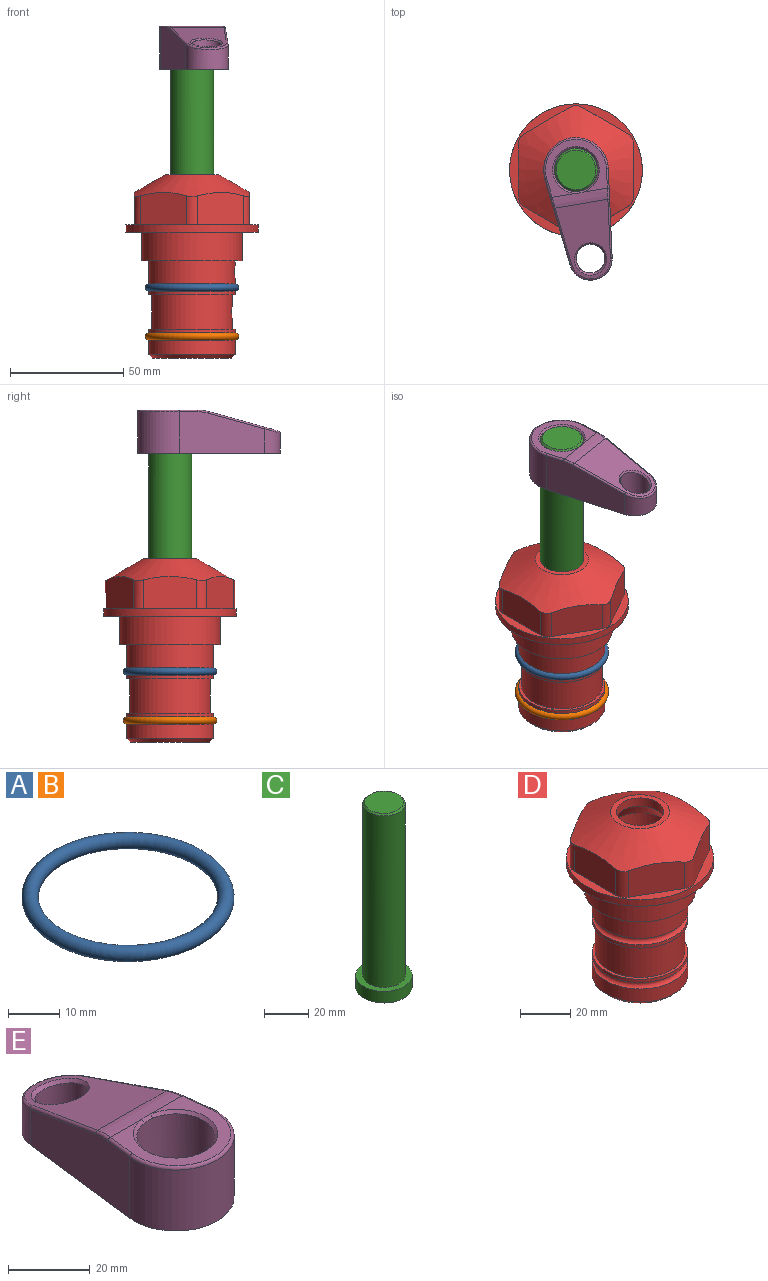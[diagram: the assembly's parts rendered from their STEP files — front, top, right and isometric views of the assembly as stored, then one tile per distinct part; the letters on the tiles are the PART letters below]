
ASSEMBLY  parts=5 mates=4
PART A: 1 faces, bbox 44.7x44.7x3.2 mm
  f0: torus R=19.05mm, axis (0,0,1), area 1193.9mm2
PART B: same geometry as A
PART C: 6 faces, bbox 25.4x25.4x101.6 mm
  f0: plane 17.46x17.46mm, normal (0,0,1), area 239.5mm2, adj f5
  f1: plane 25.4x25.4mm, normal (0,0,-1), area 506.7mm2, adj f2
  f2: cylinder r=12.7mm len=25.4mm, axis (0,0,1), area 506.7mm2, adj f1,f3
  f3: plane 25.4x25.4mm, normal (0,0,1), area 221.7mm2, adj f2,f4
  f4: cylinder r=9.53mm len=94.46mm, axis (0,0,1), area 5653mm2, adj f3,f5
  f5: cone r=8.73mm half-angle=45deg, axis (0,0,-1), area 64.4mm2, adj f0,f4
PART D: 36 faces, bbox 58.7x58.7x81 mm
  f0: cylinder r=17.78mm len=35.56mm, axis (0,0,1), area 1670.8mm2, adj f23,f24,f31
  f1: cylinder r=19.05mm len=38.1mm, axis (0,0,1), area 1191.9mm2, adj f26,f27,f30
  f2: plane 58.66x58.66mm, normal (0,0,-1), area 1150.6mm2, adj f3,f28
  f3: cylinder r=29.33mm len=58.66mm, axis (0,0,-1), area 585.1mm2, adj f2,f4
  f4: plane 58.66x58.66mm, normal (0,0,1), area 475.9mm2, adj f3,f5,f6,f7,f8,f9,f10,f11
  f5: plane 20.32x14.34mm, normal (-0.5,0.87,0), area 324.4mm2, adj f4,f15,f16,f17
  f6: plane 20.32x14.34mm, normal (0.5,0.87,0), area 324.4mm2, adj f4,f14,f15,f17
  f7: plane 23.48x14.34mm, normal (1,0,0), area 324.4mm2, adj f4,f13,f14,f17
  f8: plane 20.32x14.34mm, normal (0.5,-0.87,0), area 324.4mm2, adj f4,f12,f13,f17
  f9: plane 20.32x14.34mm, normal (-0.5,-0.87,0), area 324.4mm2, adj f4,f11,f12,f17
  f10: plane 23.48x14.34mm, normal (-1,0,0), area 324.4mm2, adj f4,f11,f16,f17
  f11: cylinder r=5.08mm len=12.85mm, axis (0,0,-1), area 67.2mm2, adj f4,f9,f10,f17
  f12: cylinder r=5.08mm len=12.85mm, axis (0,0,-1), area 67.2mm2, adj f4,f8,f9,f17
  f13: cylinder r=5.08mm len=12.85mm, axis (0,0,-1), area 67.2mm2, adj f4,f7,f8,f17
  f14: cylinder r=5.08mm len=12.85mm, axis (0,0,-1), area 67.2mm2, adj f4,f6,f7,f17
  f15: cylinder r=5.08mm len=12.85mm, axis (0,0,-1), area 67.2mm2, adj f4,f5,f6,f17
  f16: cylinder r=5.08mm len=12.85mm, axis (0,0,-1), area 67.2mm2, adj f4,f5,f10,f17
  f17: cone r=11.73mm half-angle=60deg, axis (0,0,-1), area 2071.8mm2, adj f5,f6,f7,f8,f9,f10,f11,f12
  f18: plane 23.46x23.46mm, normal (0,0,1), area 147.4mm2, adj f17,f35
  f19: plane 34.93x34.93mm, normal (0,0,-1), area 958mm2, adj f29
  f20: cylinder r=19.05mm len=38.1mm, axis (0,0,1), area 760.1mm2, adj f21,f29
  f21: torus R=19.05mm, axis (0,0,1), area 565.3mm2, adj f20,f22
  f22: cylinder r=19.05mm len=38.1mm, axis (0,0,1), area 190mm2, adj f21,f23
  f23: plane 38.1x38.1mm, normal (0,0,1), area 146.9mm2, adj f0,f22
  f24: plane 38.1x38.1mm, normal (0,0,-1), area 146.9mm2, adj f0,f25
  f25: cylinder r=19.05mm len=38.1mm, axis (0,0,1), area 190mm2, adj f24,f26
  f26: torus R=19.05mm, axis (0,0,1), area 565.3mm2, adj f1,f25
  f27: plane 44.45x44.45mm, normal (0,0,-1), area 411.7mm2, adj f1,f28
  f28: cylinder r=22.23mm len=44.45mm, axis (0,0,1), area 1773.5mm2, adj f2,f27
  f29: cone r=19.05mm half-angle=45deg, axis (0,0,1), area 257.5mm2, adj f19,f20
  f30: cylinder r=3.17mm len=6.75mm, axis (-1,0,0), area 128mm2, adj f1,f33
  f31: cylinder r=3.17mm len=6.35mm, axis (-1,0,0), area 102.5mm2, adj f0,f33
  f32: plane 25.4x25.4mm, normal (0,0,1), area 506.7mm2, adj f33
  f33: cylinder r=12.7mm len=66.42mm, axis (0,0,-1), area 5236.2mm2, adj f30,f31,f32,f34
  f34: cone r=9.53mm half-angle=30deg, axis (0,0,-1), area 443.4mm2, adj f33,f35
  f35: cylinder r=9.53mm len=19.05mm, axis (0,0,-1), area 240.9mm2, adj f18,f34
PART E: 31 faces, bbox 31.7x65.5x19.8 mm
  f0: plane 39.12x18.26mm, normal (0.99,0.12,0), area 612.2mm2, adj f1,f4,f7,f11,f13,f15
  f1: cylinder r=9.53mm len=18.91mm, axis (0,0,-1), area 296.1mm2, adj f0,f2,f7,f17
  f2: plane 39.12x18.26mm, normal (-0.99,0.12,0), area 612.2mm2, adj f1,f4,f7,f12,f14,f16
  f3: cylinder r=6.35mm len=12.7mm, axis (0,0,-1), area 362.4mm2, adj f7,f18
  f4: cylinder r=14.29mm len=28.58mm, axis (0,0,-1), area 882.2mm2, adj f0,f2,f7,f10
  f5: cylinder r=9.53mm len=19.05mm, axis (0,0,-1), area 1092.6mm2, adj f7,f19,f20
  f6: plane 26.99x23.69mm, normal (0,0,1), area 216.2mm2, adj f9,f10,f11,f12,f19
  f7: plane 63.5x28.58mm, normal (0,0,-1), area 661.8mm2, adj f0,f1,f2,f3,f4,f5,f22,f23
  f8: plane 33.52x23.6mm, normal (0,0.26,0.97), area 486mm2, adj f9,f15,f16,f17,f18
  f9: cylinder r=19.05mm len=24.72mm, axis (1,0,0), area 120.4mm2, adj f6,f8,f13,f14,f20
  f10: torus R=13.49mm, axis (0,0,1), area 59mm2, adj f4,f6,f11,f12
  f11: cylinder r=0.79mm len=8.67mm, axis (0.12,-0.99,0), area 10.8mm2, adj f0,f6,f10,f13
  f12: cylinder r=0.79mm len=8.67mm, axis (0.12,0.99,0), area 10.8mm2, adj f2,f6,f10,f14
  f13: bspline ~4.95x1.42mm, area 6.1mm2, adj f0,f9,f11,f15
  f14: bspline ~4.95x1.42mm, area 6.1mm2, adj f2,f9,f12,f16
  f15: cylinder r=0.79mm len=25.95mm, axis (0.12,-0.96,0.26), area 32.9mm2, adj f0,f8,f13,f17
  f16: cylinder r=0.79mm len=25.95mm, axis (0.12,0.96,-0.26), area 32.9mm2, adj f2,f8,f14,f17
  f17: bspline ~18.91x8.38mm, area 30mm2, adj f1,f8,f15,f16
  f18: bspline ~14.29x14.29mm, area 48.3mm2, adj f3,f8
  f19: cone r=9.53mm half-angle=45deg, axis (0,0,1), area 66.5mm2, adj f5,f6,f20
  f20: bspline ~3.22x0.96mm, area 3.5mm2, adj f5,f9,f19
  f21: plane 2.75x2.72mm, normal (0,0,-1), area 2.9mm2, adj f23,f25,f28
  f22: plane 23.05x15.88mm, normal (-0.99,-0.12,0), area 323.6mm2, adj f7,f25,f26,f27,f28,f29
  f23: plane 23.05x15.88mm, normal (0.99,-0.12,0), area 323.6mm2, adj f7,f21,f25,f27,f28,f30
  f24: cylinder r=9.53mm len=10.69mm, axis (0,0,-1), area 114.7mm2, adj f7,f27,f29,f30
  f25: cylinder r=12.7mm len=20.59mm, axis (0,0,-1), area 381.1mm2, adj f7,f21,f22,f23,f26,f28
  f26: plane 2.75x2.72mm, normal (0,0,-1), area 2.9mm2, adj f22,f25,f28
  f27: plane 19.72x18.37mm, normal (0,-0.26,-0.97), area 291.8mm2, adj f22,f23,f24,f28,f29,f30
  f28: cylinder r=15.88mm len=19.92mm, axis (1,0,0), area 54.8mm2, adj f21,f22,f23,f25,f26,f27
  f29: cylinder r=1.59mm len=11mm, axis (0,0,-1), area 34.7mm2, adj f7,f22,f24,f27
  f30: cylinder r=1.59mm len=11mm, axis (0,0,-1), area 34.7mm2, adj f7,f23,f24,f27
PLACE A at identity
PLACE B t=(0,0,-21.59)mm
PLACE C rot(axis=(0,0,-1),170.6deg) t=(0,0,27.55)mm
PLACE D at identity fixed
PLACE E rot(axis=(0,0,-1),170.6deg) t=(0,0,27.55)mm
MATE fastened E.f4 <-> C.f2  axis (0,0,1) through (0,0,91.05)mm
MATE cylindrical C.f2 <-> D.f0  axis (0,0,-1) through (0,0,-10.55)mm
MATE fastened D.f0 <-> B.f0  axis (0,0,1) through (0,0,-46.1)mm
MATE fastened D.f0 <-> A.f0  axis (0,0,1) through (0,0,-24.51)mm
